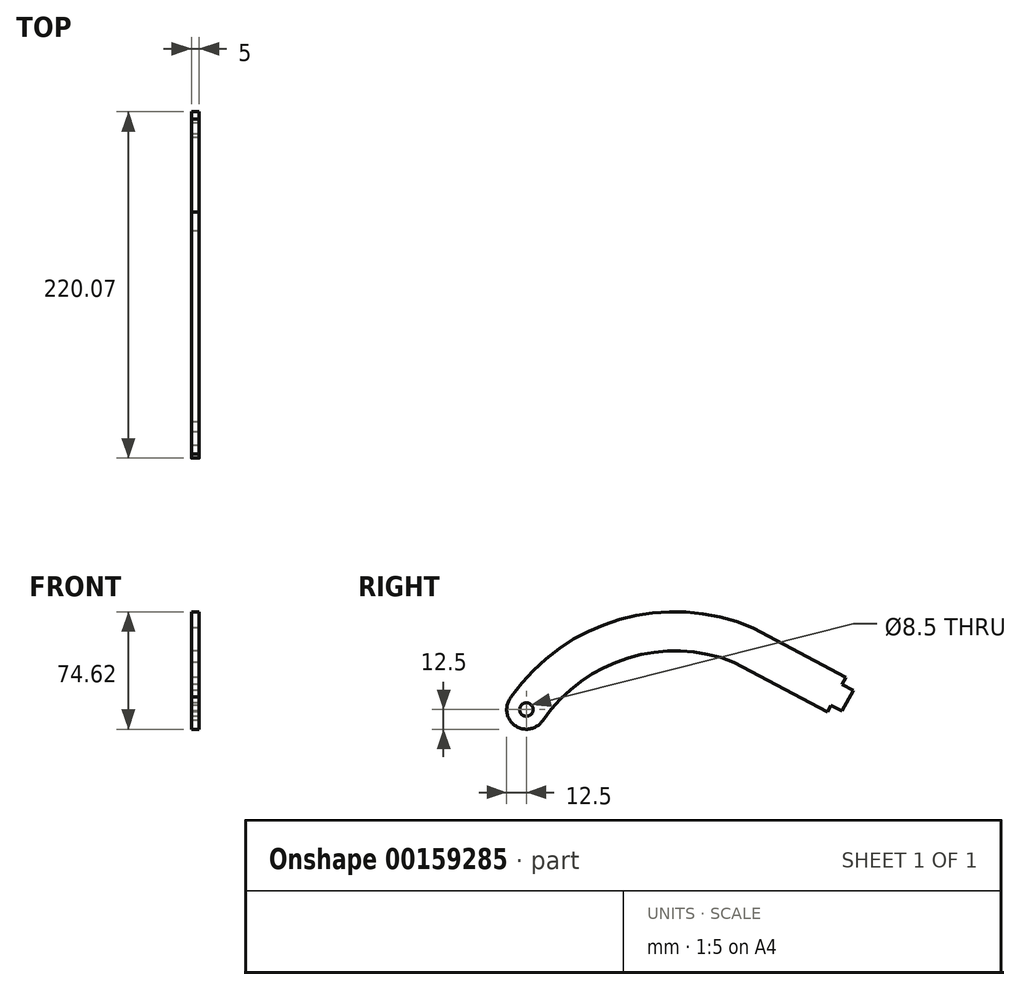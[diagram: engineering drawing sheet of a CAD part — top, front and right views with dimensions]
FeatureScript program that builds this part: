
annotation { "Feature Type Name" : "Feature", "Feature Type Description" : "" }
export const myFeature = defineFeature(function(context is Context, id is Id, definition is map)
    precondition{}
    {
        {
            var Q0;
            Q0=qCreatedBy(makeId("Right.planeOp"),FACE);
            var sketch = newSketch(context, id + "F0", { "sketchPlane" : qUnion([Q0])});
            skCircle(sketch, "E0", {"center": v(0, 0) * mm, "radius": 4.25 * mm});
            skLineSegment(sketch, "E1", {"start": v(0, 0) * mm, "end": v(188, 0) * mm});
            skLineSegment(sketch, "E2", {"start": v(0, 0) * mm, "end": v(199.79, 22.05) * mm});
            skLineSegment(sketch, "E3", {"start": v(199.79, 22.05) * mm, "end": v(188, 0) * mm});
            skCircle(sketch, "E4", {"center": v(0, 0) * mm, "radius": 12.5 * mm});
            skLineSegment(sketch, "E5", {"start": v(199.79, 22.05) * mm, "end": v(143.87, 51.94) * mm});
            skLineSegment(sketch, "E6", {"start": v(188, 0) * mm, "end": v(131.8, 30.05) * mm});
            skArc(sketch, "E7", {"start": v(143.87, 51.94) * mm, "mid": v(59.28, 57.22) * mm, "end": v(-9.67, 7.92) * mm});
            skArc(sketch, "E8", {"start": v(131.8, 30.05) * mm, "mid": v(64.44, 32.69) * mm, "end": v(10.16, -7.29) * mm});
            skLineSegment(sketch, "E9", {"start": v(197.43, 17.64) * mm, "end": v(207.57, 12.22) * mm});
            skLineSegment(sketch, "E10", {"start": v(207.57, 12.22) * mm, "end": v(200.5, -1.01) * mm});
            skLineSegment(sketch, "E11", {"start": v(200.5, -1.01) * mm, "end": v(190.36, 4.4) * mm});
            skLineSegment(sketch, "E12", {"start": v(199.79, 22.05) * mm, "end": v(202.87, 20.4) * mm});
            skLineSegment(sketch, "E13", {"start": v(188, 0) * mm, "end": v(191.09, -1.65) * mm});
            skLineSegment(sketch, "E14", {"start": v(191.09, -1.65) * mm, "end": v(202.87, 20.4) * mm});
            skSolve(sketch);
        }
        {
            var Q0;
            {var subQ0=sQuery(id+"F0.wireOp",EDGE,"E9");Q0=makeQuery(id+"F0.imprint","IMPRINT",FACE,{"disambiguationData":[TD([[makeQuery(id+"F0.imprint","IMPRINT",EDGE,{"derivedFrom":subQ0}),-1.0]])]});}
            var Q1;
            {var subQ0=sQuery(id+"F0.wireOp",EDGE,"E8");var subQ1=sQuery(id+"F0.wireOp",EDGE,"E4");var subQ2=makeQuery(id+"F0.imprint","INTERSECT",VERTEX,{"disambiguationData":[OD(0.0)],"derivedFrom":[subQ1,subQ0]});Q1=makeQuery(id+"F0.imprint","IMPRINT",FACE,{"disambiguationData":[TD([[makeQuery(id+"F0.imprint","IMPRINT",EDGE,{"disambiguationData":[TD([[subQ2,-1.0]])],"derivedFrom":subQ1}),1.0]])]});}
            var Q2;
            {var subQ0=sQuery(id+"F0.wireOp",EDGE,"E8");var subQ1=sQuery(id+"F0.wireOp",EDGE,"E1");var subQ2=makeQuery(id+"F0.imprint","INTERSECT",VERTEX,{"derivedFrom":[subQ1,subQ0]});Q2=makeQuery(id+"F0.imprint","IMPRINT",FACE,{"disambiguationData":[TD([[makeQuery(id+"F0.imprint","IMPRINT",EDGE,{"disambiguationData":[TD([[subQ2,1.0]])],"derivedFrom":subQ1}),-1.0]])]});}
            var Q3;
            {var subQ1=sQuery(id+"F0.wireOp",EDGE,"E3");var subQ4=makeQuery(id+"F0.imprint","INTERSECT",VERTEX,{"derivedFrom":[subQ1,sQuery(id+"F0.wireOp",EDGE,"E9")]});Q3=makeQuery(id+"F0.imprint","IMPRINT",FACE,{"disambiguationData":[TD([[makeQuery(id+"F0.imprint","IMPRINT",EDGE,{"disambiguationData":[TD([[subQ4,-1.0]])],"derivedFrom":subQ1}),-1.0]])]});}
            var Q4;
            {var subQ0=sQuery(id+"F0.wireOp",EDGE,"E8");var subQ1=sQuery(id+"F0.wireOp",EDGE,"E1");var subQ2=makeQuery(id+"F0.imprint","INTERSECT",VERTEX,{"derivedFrom":[subQ1,subQ0]});Q4=makeQuery(id+"F0.imprint","IMPRINT",FACE,{"disambiguationData":[TD([[makeQuery(id+"F0.imprint","IMPRINT",EDGE,{"disambiguationData":[TD([[subQ2,1.0]])],"derivedFrom":subQ1}),1.0]])]});}
            var Q5;
            {var subQ0=sQuery(id+"F0.wireOp",EDGE,"E5");Q5=makeQuery(id+"F0.imprint","IMPRINT",FACE,{"disambiguationData":[TD([[makeQuery(id+"F0.imprint","IMPRINT",EDGE,{"derivedFrom":subQ0}),1.0]])]});}
            var Q6;
            {var subQ7=sQuery(id+"F0.wireOp",EDGE,"E0");var subQ9=sQuery(id+"F0.wireOp",EDGE,"E1");var subQ11=makeQuery(id+"F0.imprint","INTERSECT",VERTEX,{"derivedFrom":[subQ7,subQ9]});Q6=makeQuery(id+"F0.imprint","IMPRINT",FACE,{"disambiguationData":[TD([[makeQuery(id+"F0.imprint","IMPRINT",EDGE,{"disambiguationData":[TD([[subQ11,1.0]])],"derivedFrom":subQ7}),-1.0]])]});}
            var Q7;
            {var subQ0=sQuery(id+"F0.wireOp",EDGE,"E1");var subQ1=sQuery(id+"F0.wireOp",EDGE,"E0");var subQ2=makeQuery(id+"F0.imprint","INTERSECT",VERTEX,{"derivedFrom":[subQ1,subQ0]});Q7=makeQuery(id+"F0.imprint","IMPRINT",FACE,{"disambiguationData":[TD([[makeQuery(id+"F0.imprint","IMPRINT",EDGE,{"disambiguationData":[TD([[subQ2,-1.0]])],"derivedFrom":subQ1}),-1.0]])]});}
            var Q8;
            {var subQ0=sQuery(id+"F0.wireOp",EDGE,"E12");Q8=makeQuery(id+"F0.imprint","IMPRINT",FACE,{"disambiguationData":[TD([[makeQuery(id+"F0.imprint","IMPRINT",EDGE,{"derivedFrom":subQ0}),-1.0]])]});}
            var Q9;
            {var subQ0=sQuery(id+"F0.wireOp",EDGE,"E13");Q9=makeQuery(id+"F0.imprint","IMPRINT",FACE,{"disambiguationData":[TD([[makeQuery(id+"F0.imprint","IMPRINT",EDGE,{"derivedFrom":subQ0}),1.0]])]});}
            extrude(context, id + "F1", {"entities" : qUnion([Q0, Q1, Q2, Q3, Q4, Q5, Q6, Q7, Q8, Q9]), "depth" : 5 * mm});
        }
    });
